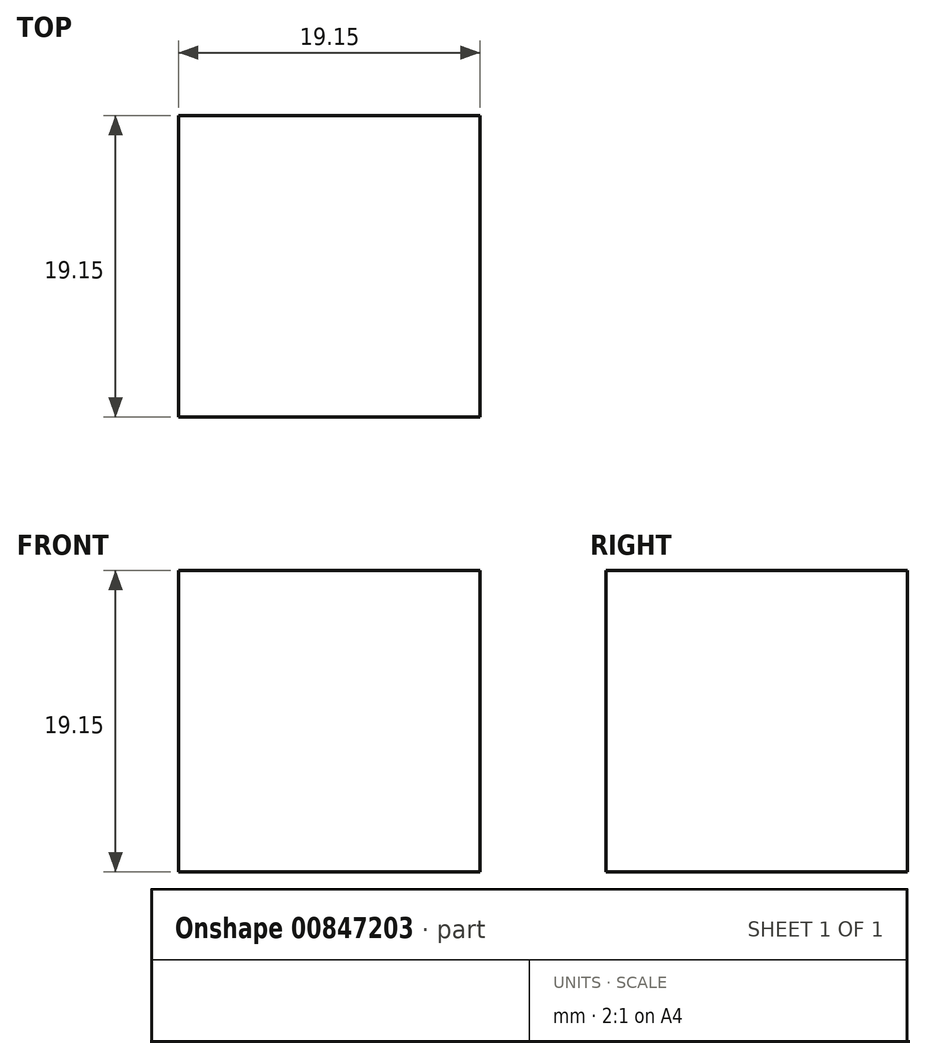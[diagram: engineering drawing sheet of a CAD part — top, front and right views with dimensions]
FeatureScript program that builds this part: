
annotation { "Feature Type Name" : "Feature", "Feature Type Description" : "" }
export const myFeature = defineFeature(function(context is Context, id is Id, definition is map)
    precondition{}
    {
        {
            var Q0;
            Q0=qCreatedBy(makeId("Front.planeOp"),FACE);
            var sketch = newSketch(context, id + "F0", { "sketchPlane" : qUnion([Q0])});
            skLineSegment(sketch, "E0.bottom", {"start": v(-27.83, 68.7) * mm, "end": v(-8.68, 68.7) * mm});
            skLineSegment(sketch, "E0.top", {"start": v(-27.83, 49.56) * mm, "end": v(-8.68, 49.56) * mm});
            skLineSegment(sketch, "E0.left", {"start": v(-27.83, 68.7) * mm, "end": v(-27.83, 49.56) * mm});
            skLineSegment(sketch, "E0.right", {"start": v(-8.68, 68.7) * mm, "end": v(-8.68, 49.56) * mm});
            skSolve(sketch);
        }
        {
            var Q0;
            Q0=makeQuery(id+"F0.imprint","IMPRINT",FACE,{"disambiguationData":[TD([[makeQuery(id+"F0.imprint","IMPRINT",EDGE,{"derivedFrom":sQuery(id+"F0.wireOp",EDGE,"E0.bottom")}),-1.0]])]});
            extrude(context, id + "F1", {"entities" : qUnion([Q0]), "depth" : 19.15 * mm, "offsetDistance" : 25.4 * mm});
        }
    });
